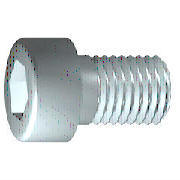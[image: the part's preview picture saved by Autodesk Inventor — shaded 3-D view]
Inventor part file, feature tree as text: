
AUTODESK INVENTOR PART (.ipt)
format: ipt  version: 2021 (Build 250183000, 183)  size: 195,584 bytes
history: native  units: mm (DEFAULTED — no unit token found)
features: sketch x2, extrude x1, plane x1, fillet x1
ambient origin geometry x7: Origin, YZ Plane, XY Plane, X Axis, Y Axis, Z Axis, Center Point
bodies: Solid1 (feature_tree), Body (feature_tree)
feature tree (5):
  extrude  "Slot"  Depth=2.0mm
  plane  "Work Plane1"
  fillet  "Fillet2"  Radius=2.0mm
  sketch  "Sketch1"  dims[d1=5.0mm d2=0.24548mm d3=2.0mm]
  sketch  "Sketch2"  dims[d4=1.0mm d5=60.0deg d6=2.0mm d7=2.0mm d8=1.732051mm d9=3.8mm d10=90.0deg d11=10.0mm d12=0.0mm d13=5.0mm d14=0.0mm d15=0.24538mm d16=0.24538mm d17=0.2mm d19=0.0mm d26=6.0mm d27=45.0deg d28=0.0mm d29=0.0mm d30=0.1mm]
